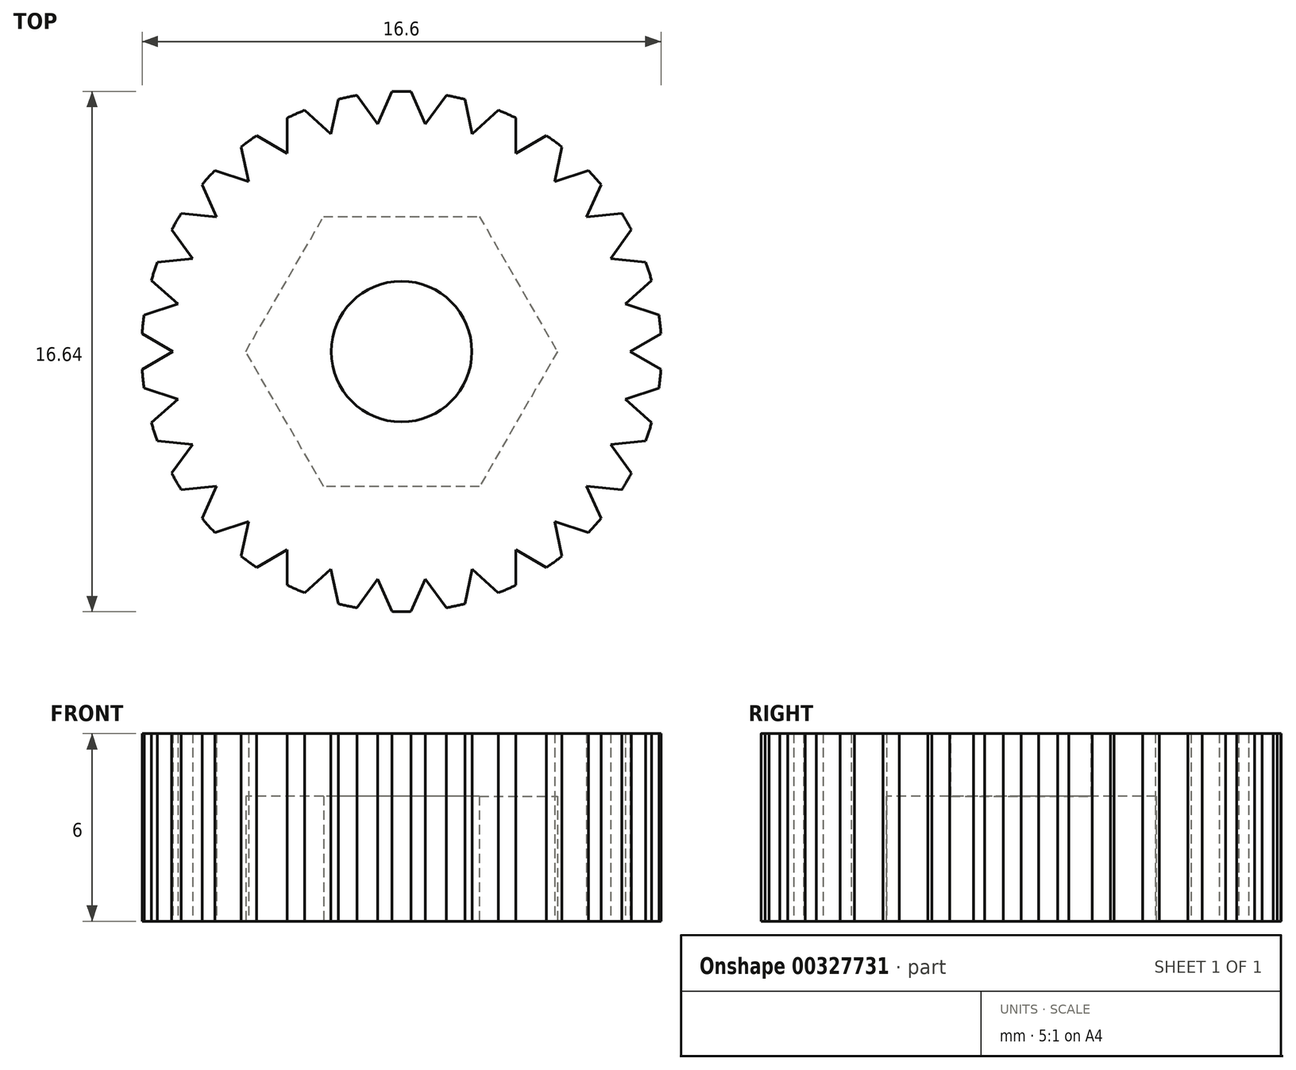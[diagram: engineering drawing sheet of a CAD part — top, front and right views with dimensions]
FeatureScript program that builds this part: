
annotation { "Feature Type Name" : "Feature", "Feature Type Description" : "" }
export const myFeature = defineFeature(function(context is Context, id is Id, definition is map)
    precondition{}
    {
        {
            var Q0;
            Q0=qCreatedBy(makeId("Top.planeOp"),FACE);
            var sketch = newSketch(context, id + "F0", { "sketchPlane" : qUnion([Q0])});
            skCircle(sketch, "E0", {"center": v(0, 0) * mm, "radius": 8.32 * mm});
            skCircle(sketch, "E1.cCircle", {"center": v(0, 0) * mm, "radius": 4.32 * mm, "construction": true});
            skLineSegment(sketch, "E1.0", {"start": v(4.99, 0) * mm, "end": v(2.5, -4.32) * mm});
            skLineSegment(sketch, "E1.1", {"start": v(2.5, -4.32) * mm, "end": v(-2.5, -4.32) * mm});
            skLineSegment(sketch, "E1.2", {"start": v(-2.5, -4.32) * mm, "end": v(-4.99, 0) * mm});
            skLineSegment(sketch, "E1.3", {"start": v(-4.99, 0) * mm, "end": v(-2.5, 4.32) * mm});
            skLineSegment(sketch, "E1.4", {"start": v(-2.5, 4.32) * mm, "end": v(2.5, 4.32) * mm});
            skLineSegment(sketch, "E1.5", {"start": v(2.5, 4.32) * mm, "end": v(4.99, 0) * mm});
            skPoint(sketch, "E1.0.midPoint", {"position": v(3.74, -2.16) * mm});
            skSolve(sketch);
        }
        {
            var Q0;
            Q0=makeQuery(id+"F0.imprint","IMPRINT",FACE,{"disambiguationData":[TD([[makeQuery(id+"F0.imprint","IMPRINT",EDGE,{"derivedFrom":sQuery(id+"F0.wireOp",EDGE,"E0")}),1.0]])]});
            extrude(context, id + "F1", {"entities" : qUnion([Q0]), "depth" : 6 * mm});
        }
        {
            var Q0;
            Q0=makeQuery(id+"F1.opExtrude","CAP_FACE",FACE,{"disambiguationData":[OSD([sQuery(id+"F0.wireOp",EDGE,"E0"),sQuery(id+"F0.wireOp",EDGE,"E1.0"),sQuery(id+"F0.wireOp",EDGE,"E1.1"),sQuery(id+"F0.wireOp",EDGE,"E1.2"),sQuery(id+"F0.wireOp",EDGE,"E1.3"),sQuery(id+"F0.wireOp",EDGE,"E1.4"),sQuery(id+"F0.wireOp",EDGE,"E1.5")])],"isStart":false});
            var sketch = newSketch(context, id + "F2", { "sketchPlane" : qUnion([Q0])});
            skLineSegment(sketch, "E2.0", {"start": v(-2.5, -4.32) * mm, "end": v(-4.99, 0) * mm});
            skLineSegment(sketch, "E3.0", {"start": v(2.5, -4.32) * mm, "end": v(-2.5, -4.32) * mm});
            skLineSegment(sketch, "E4.0", {"start": v(4.99, 0) * mm, "end": v(2.5, -4.32) * mm});
            skLineSegment(sketch, "E5.0", {"start": v(2.5, 4.32) * mm, "end": v(4.99, 0) * mm});
            skLineSegment(sketch, "E6.0", {"start": v(-2.5, 4.32) * mm, "end": v(2.5, 4.32) * mm});
            skLineSegment(sketch, "E7.0", {"start": v(-4.99, 0) * mm, "end": v(-2.5, 4.32) * mm});
            skCircle(sketch, "E8", {"center": v(0, 0) * mm, "radius": 2.25 * mm});
            skSolve(sketch);
        }
        {
            var Q0;
            Q0=qSketchRegion(id+"F2",true);
            extrude(context, id + "F3", {"entities" : qUnion([Q0]), "operationType" : NewBodyOperationType.ADD, "oppositeDirection" : true, "depth" : 2 * mm});
        }
        {
            var Q0;
            Q0=makeQuery(id+"F1.opExtrude","CAP_FACE",FACE,{"disambiguationData":[OSD([sQuery(id+"F0.wireOp",EDGE,"E0"),sQuery(id+"F0.wireOp",EDGE,"E1.0"),sQuery(id+"F0.wireOp",EDGE,"E1.1"),sQuery(id+"F0.wireOp",EDGE,"E1.2"),sQuery(id+"F0.wireOp",EDGE,"E1.3"),sQuery(id+"F0.wireOp",EDGE,"E1.4"),sQuery(id+"F0.wireOp",EDGE,"E1.5")])],"isStart":true});
            var sketch = newSketch(context, id + "F4", { "sketchPlane" : qUnion([Q0])});
            skLineSegment(sketch, "E9", {"start": v(-9.05, -1) * mm, "end": v(-7.32, 0) * mm});
            skLineSegment(sketch, "E10", {"start": v(-7.32, 0) * mm, "end": v(-9.05, 1) * mm});
            skLineSegment(sketch, "E11", {"start": v(-9.05, 1) * mm, "end": v(-9.05, -1) * mm});
            skLineSegment(sketch, "E12", {"start": v(0, 0) * mm, "end": v(-9.05, 0) * mm, "construction": true});
            skPoint(sketch, "E13.center", {"position": v(0, 0) * mm});
            skLineSegment(sketch, "E13.anchor1", {"start": v(0, 0) * mm, "end": v(-9.05, -1) * mm, "construction": true});
            skLineSegment(sketch, "E13.anchor2", {"start": v(0, 0) * mm, "end": v(-9.05, -1) * mm, "construction": true});
            skSolve(sketch);
        }
        {
            var Q0;
            Q0=qSketchRegion(id+"F4",true);
            extrude(context, id + "F5", {"entities" : qUnion([Q0]), "oppositeDirection" : true, "depth" : 6 * mm});
        }
        {
            var Q0;
            Q0=makeQuery(id+"F5.opExtrude","SWEPT_BODY",BODY,{"disambiguationData":[OSD([sQuery(id+"F4.wireOp",EDGE,"E9"),sQuery(id+"F4.wireOp",EDGE,"E10"),sQuery(id+"F4.wireOp",EDGE,"E11")])]});
            var Q1;
            Q1=makeQuery(id+"F3.opExtrude","CAP_EDGE",EDGE,{"disambiguationData":[OSD([sQuery(id+"F2.wireOp",EDGE,"E8")])],"isStart":true});
            circularPattern(context, id + "F6", {"entities" : qUnion([Q0]), "axis" : qUnion([Q1]), "angle" : 360 * degree, "instanceCount" : 30, "equalSpace" : true});
        }
        {
            var Q0;
            Q0=makeQuery(id+"F5.opExtrude","SWEPT_BODY",BODY,{"disambiguationData":[OSD([sQuery(id+"F4.wireOp",EDGE,"E9"),sQuery(id+"F4.wireOp",EDGE,"E10"),sQuery(id+"F4.wireOp",EDGE,"E11")])]});
            var Q1;
            Q1=makeQuery(id+"F6.opPattern","COPY",BODY,{"derivedFrom":makeQuery(id+"F5.opExtrude","SWEPT_BODY",BODY,{"disambiguationData":[OSD([sQuery(id+"F4.wireOp",EDGE,"E9"),sQuery(id+"F4.wireOp",EDGE,"E10"),sQuery(id+"F4.wireOp",EDGE,"E11")])]}),"instanceName":"1"});
            var Q2;
            Q2=makeQuery(id+"F6.opPattern","COPY",BODY,{"derivedFrom":makeQuery(id+"F5.opExtrude","SWEPT_BODY",BODY,{"disambiguationData":[OSD([sQuery(id+"F4.wireOp",EDGE,"E9"),sQuery(id+"F4.wireOp",EDGE,"E10"),sQuery(id+"F4.wireOp",EDGE,"E11")])]}),"instanceName":"2"});
            var Q3;
            Q3=makeQuery(id+"F6.opPattern","COPY",BODY,{"derivedFrom":makeQuery(id+"F5.opExtrude","SWEPT_BODY",BODY,{"disambiguationData":[OSD([sQuery(id+"F4.wireOp",EDGE,"E9"),sQuery(id+"F4.wireOp",EDGE,"E10"),sQuery(id+"F4.wireOp",EDGE,"E11")])]}),"instanceName":"3"});
            var Q4;
            Q4=makeQuery(id+"F6.opPattern","COPY",BODY,{"derivedFrom":makeQuery(id+"F5.opExtrude","SWEPT_BODY",BODY,{"disambiguationData":[OSD([sQuery(id+"F4.wireOp",EDGE,"E9"),sQuery(id+"F4.wireOp",EDGE,"E10"),sQuery(id+"F4.wireOp",EDGE,"E11")])]}),"instanceName":"4"});
            var Q5;
            Q5=makeQuery(id+"F6.opPattern","COPY",BODY,{"derivedFrom":makeQuery(id+"F5.opExtrude","SWEPT_BODY",BODY,{"disambiguationData":[OSD([sQuery(id+"F4.wireOp",EDGE,"E9"),sQuery(id+"F4.wireOp",EDGE,"E10"),sQuery(id+"F4.wireOp",EDGE,"E11")])]}),"instanceName":"5"});
            var Q6;
            Q6=makeQuery(id+"F6.opPattern","COPY",BODY,{"derivedFrom":makeQuery(id+"F5.opExtrude","SWEPT_BODY",BODY,{"disambiguationData":[OSD([sQuery(id+"F4.wireOp",EDGE,"E9"),sQuery(id+"F4.wireOp",EDGE,"E10"),sQuery(id+"F4.wireOp",EDGE,"E11")])]}),"instanceName":"6"});
            var Q7;
            Q7=makeQuery(id+"F6.opPattern","COPY",BODY,{"derivedFrom":makeQuery(id+"F5.opExtrude","SWEPT_BODY",BODY,{"disambiguationData":[OSD([sQuery(id+"F4.wireOp",EDGE,"E9"),sQuery(id+"F4.wireOp",EDGE,"E10"),sQuery(id+"F4.wireOp",EDGE,"E11")])]}),"instanceName":"7"});
            var Q8;
            Q8=makeQuery(id+"F6.opPattern","COPY",BODY,{"derivedFrom":makeQuery(id+"F5.opExtrude","SWEPT_BODY",BODY,{"disambiguationData":[OSD([sQuery(id+"F4.wireOp",EDGE,"E9"),sQuery(id+"F4.wireOp",EDGE,"E10"),sQuery(id+"F4.wireOp",EDGE,"E11")])]}),"instanceName":"8"});
            var Q9;
            Q9=makeQuery(id+"F6.opPattern","COPY",BODY,{"derivedFrom":makeQuery(id+"F5.opExtrude","SWEPT_BODY",BODY,{"disambiguationData":[OSD([sQuery(id+"F4.wireOp",EDGE,"E9"),sQuery(id+"F4.wireOp",EDGE,"E10"),sQuery(id+"F4.wireOp",EDGE,"E11")])]}),"instanceName":"9"});
            var Q10;
            Q10=makeQuery(id+"F6.opPattern","COPY",BODY,{"derivedFrom":makeQuery(id+"F5.opExtrude","SWEPT_BODY",BODY,{"disambiguationData":[OSD([sQuery(id+"F4.wireOp",EDGE,"E9"),sQuery(id+"F4.wireOp",EDGE,"E10"),sQuery(id+"F4.wireOp",EDGE,"E11")])]}),"instanceName":"10"});
            var Q11;
            Q11=makeQuery(id+"F6.opPattern","COPY",BODY,{"derivedFrom":makeQuery(id+"F5.opExtrude","SWEPT_BODY",BODY,{"disambiguationData":[OSD([sQuery(id+"F4.wireOp",EDGE,"E9"),sQuery(id+"F4.wireOp",EDGE,"E10"),sQuery(id+"F4.wireOp",EDGE,"E11")])]}),"instanceName":"11"});
            var Q12;
            Q12=makeQuery(id+"F6.opPattern","COPY",BODY,{"derivedFrom":makeQuery(id+"F5.opExtrude","SWEPT_BODY",BODY,{"disambiguationData":[OSD([sQuery(id+"F4.wireOp",EDGE,"E9"),sQuery(id+"F4.wireOp",EDGE,"E10"),sQuery(id+"F4.wireOp",EDGE,"E11")])]}),"instanceName":"12"});
            var Q13;
            Q13=makeQuery(id+"F6.opPattern","COPY",BODY,{"derivedFrom":makeQuery(id+"F5.opExtrude","SWEPT_BODY",BODY,{"disambiguationData":[OSD([sQuery(id+"F4.wireOp",EDGE,"E9"),sQuery(id+"F4.wireOp",EDGE,"E10"),sQuery(id+"F4.wireOp",EDGE,"E11")])]}),"instanceName":"13"});
            var Q14;
            Q14=makeQuery(id+"F6.opPattern","COPY",BODY,{"derivedFrom":makeQuery(id+"F5.opExtrude","SWEPT_BODY",BODY,{"disambiguationData":[OSD([sQuery(id+"F4.wireOp",EDGE,"E9"),sQuery(id+"F4.wireOp",EDGE,"E10"),sQuery(id+"F4.wireOp",EDGE,"E11")])]}),"instanceName":"14"});
            var Q15;
            Q15=makeQuery(id+"F6.opPattern","COPY",BODY,{"derivedFrom":makeQuery(id+"F5.opExtrude","SWEPT_BODY",BODY,{"disambiguationData":[OSD([sQuery(id+"F4.wireOp",EDGE,"E9"),sQuery(id+"F4.wireOp",EDGE,"E10"),sQuery(id+"F4.wireOp",EDGE,"E11")])]}),"instanceName":"15"});
            var Q16;
            Q16=makeQuery(id+"F6.opPattern","COPY",BODY,{"derivedFrom":makeQuery(id+"F5.opExtrude","SWEPT_BODY",BODY,{"disambiguationData":[OSD([sQuery(id+"F4.wireOp",EDGE,"E9"),sQuery(id+"F4.wireOp",EDGE,"E10"),sQuery(id+"F4.wireOp",EDGE,"E11")])]}),"instanceName":"16"});
            var Q17;
            Q17=makeQuery(id+"F6.opPattern","COPY",BODY,{"derivedFrom":makeQuery(id+"F5.opExtrude","SWEPT_BODY",BODY,{"disambiguationData":[OSD([sQuery(id+"F4.wireOp",EDGE,"E9"),sQuery(id+"F4.wireOp",EDGE,"E10"),sQuery(id+"F4.wireOp",EDGE,"E11")])]}),"instanceName":"17"});
            var Q18;
            Q18=makeQuery(id+"F6.opPattern","COPY",BODY,{"derivedFrom":makeQuery(id+"F5.opExtrude","SWEPT_BODY",BODY,{"disambiguationData":[OSD([sQuery(id+"F4.wireOp",EDGE,"E9"),sQuery(id+"F4.wireOp",EDGE,"E10"),sQuery(id+"F4.wireOp",EDGE,"E11")])]}),"instanceName":"18"});
            var Q19;
            Q19=makeQuery(id+"F6.opPattern","COPY",BODY,{"derivedFrom":makeQuery(id+"F5.opExtrude","SWEPT_BODY",BODY,{"disambiguationData":[OSD([sQuery(id+"F4.wireOp",EDGE,"E9"),sQuery(id+"F4.wireOp",EDGE,"E10"),sQuery(id+"F4.wireOp",EDGE,"E11")])]}),"instanceName":"19"});
            var Q20;
            Q20=makeQuery(id+"F6.opPattern","COPY",BODY,{"derivedFrom":makeQuery(id+"F5.opExtrude","SWEPT_BODY",BODY,{"disambiguationData":[OSD([sQuery(id+"F4.wireOp",EDGE,"E9"),sQuery(id+"F4.wireOp",EDGE,"E10"),sQuery(id+"F4.wireOp",EDGE,"E11")])]}),"instanceName":"20"});
            var Q21;
            Q21=makeQuery(id+"F6.opPattern","COPY",BODY,{"derivedFrom":makeQuery(id+"F5.opExtrude","SWEPT_BODY",BODY,{"disambiguationData":[OSD([sQuery(id+"F4.wireOp",EDGE,"E9"),sQuery(id+"F4.wireOp",EDGE,"E10"),sQuery(id+"F4.wireOp",EDGE,"E11")])]}),"instanceName":"21"});
            var Q22;
            Q22=makeQuery(id+"F6.opPattern","COPY",BODY,{"derivedFrom":makeQuery(id+"F5.opExtrude","SWEPT_BODY",BODY,{"disambiguationData":[OSD([sQuery(id+"F4.wireOp",EDGE,"E9"),sQuery(id+"F4.wireOp",EDGE,"E10"),sQuery(id+"F4.wireOp",EDGE,"E11")])]}),"instanceName":"22"});
            var Q23;
            Q23=makeQuery(id+"F6.opPattern","COPY",BODY,{"derivedFrom":makeQuery(id+"F5.opExtrude","SWEPT_BODY",BODY,{"disambiguationData":[OSD([sQuery(id+"F4.wireOp",EDGE,"E9"),sQuery(id+"F4.wireOp",EDGE,"E10"),sQuery(id+"F4.wireOp",EDGE,"E11")])]}),"instanceName":"23"});
            var Q24;
            Q24=makeQuery(id+"F6.opPattern","COPY",BODY,{"derivedFrom":makeQuery(id+"F5.opExtrude","SWEPT_BODY",BODY,{"disambiguationData":[OSD([sQuery(id+"F4.wireOp",EDGE,"E9"),sQuery(id+"F4.wireOp",EDGE,"E10"),sQuery(id+"F4.wireOp",EDGE,"E11")])]}),"instanceName":"24"});
            var Q25;
            Q25=makeQuery(id+"F6.opPattern","COPY",BODY,{"derivedFrom":makeQuery(id+"F5.opExtrude","SWEPT_BODY",BODY,{"disambiguationData":[OSD([sQuery(id+"F4.wireOp",EDGE,"E9"),sQuery(id+"F4.wireOp",EDGE,"E10"),sQuery(id+"F4.wireOp",EDGE,"E11")])]}),"instanceName":"25"});
            var Q26;
            Q26=makeQuery(id+"F6.opPattern","COPY",BODY,{"derivedFrom":makeQuery(id+"F5.opExtrude","SWEPT_BODY",BODY,{"disambiguationData":[OSD([sQuery(id+"F4.wireOp",EDGE,"E9"),sQuery(id+"F4.wireOp",EDGE,"E10"),sQuery(id+"F4.wireOp",EDGE,"E11")])]}),"instanceName":"26"});
            var Q27;
            Q27=makeQuery(id+"F6.opPattern","COPY",BODY,{"derivedFrom":makeQuery(id+"F5.opExtrude","SWEPT_BODY",BODY,{"disambiguationData":[OSD([sQuery(id+"F4.wireOp",EDGE,"E9"),sQuery(id+"F4.wireOp",EDGE,"E10"),sQuery(id+"F4.wireOp",EDGE,"E11")])]}),"instanceName":"27"});
            var Q28;
            Q28=makeQuery(id+"F6.opPattern","COPY",BODY,{"derivedFrom":makeQuery(id+"F5.opExtrude","SWEPT_BODY",BODY,{"disambiguationData":[OSD([sQuery(id+"F4.wireOp",EDGE,"E9"),sQuery(id+"F4.wireOp",EDGE,"E10"),sQuery(id+"F4.wireOp",EDGE,"E11")])]}),"instanceName":"28"});
            var Q29;
            Q29=makeQuery(id+"F6.opPattern","COPY",BODY,{"derivedFrom":makeQuery(id+"F5.opExtrude","SWEPT_BODY",BODY,{"disambiguationData":[OSD([sQuery(id+"F4.wireOp",EDGE,"E9"),sQuery(id+"F4.wireOp",EDGE,"E10"),sQuery(id+"F4.wireOp",EDGE,"E11")])]}),"instanceName":"29"});
            var Q30;
            Q30=makeQuery(id+"F1.opExtrude","SWEPT_BODY",BODY,{"disambiguationData":[OSD([sQuery(id+"F0.wireOp",EDGE,"E0"),sQuery(id+"F0.wireOp",EDGE,"E1.0"),sQuery(id+"F0.wireOp",EDGE,"E1.1"),sQuery(id+"F0.wireOp",EDGE,"E1.2"),sQuery(id+"F0.wireOp",EDGE,"E1.3"),sQuery(id+"F0.wireOp",EDGE,"E1.4"),sQuery(id+"F0.wireOp",EDGE,"E1.5")])]});
            booleanBodies(context, id + "F7", {"operationType" : BooleanOperationType.SUBTRACTION, "tools" : qUnion([Q0, Q1, Q2, Q3, Q4, Q5, Q6, Q7, Q8, Q9, Q10, Q11, Q12, Q13, Q14, Q15, Q16, Q17, Q18, Q19, Q20, Q21, Q22, Q23, Q24, Q25, Q26, Q27, Q28, Q29]), "targets" : qUnion([Q30])});
        }
    });
